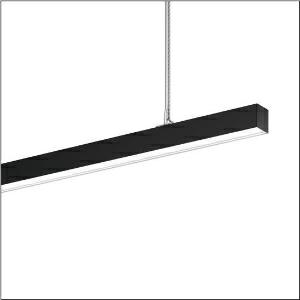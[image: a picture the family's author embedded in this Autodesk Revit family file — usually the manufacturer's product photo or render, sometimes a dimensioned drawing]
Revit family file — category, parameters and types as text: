
# Revit family: silica_r__21_51mx30tbt5b_11dd
name_source: partatom
category: Lighting Fixtures
units: mm (PartAtom-declared; Revit-internal decimal feet)

## family parameters
Cut with Voids When Loaded = No
Host = Face
Light Source = No
Part Type = Normal
Room Calculation Point = No
Round Connector Dimension = Use Diameter
Shared = No

## types (1)
- --- (1 x LED, 5150 lm, 42.2 W, 6500K)
    Apparent Load = 42 VA
    CIE Flux Codes = 47 79 96 58 100
    Color Rendering = 80
    Color Temperature = 6500K
    Default Elevation = 1800 mm
    Description = Silica® 21, office luminaire, primary optical cover: cover, of PMMA, opal, light emission: direct/indirect distribution, primary light characteristic: symmetric, installation type: suspended mounting, LED, rated luminous flux: 5.150lm, luminous efficacy: 116lm/W, light colour: 8tw, colour temperature: 2700..6500K, control gear: ECG DALI, with terminal, 3+2-pole, max. 2.5mm², mains connection: 220..240V, AC, 50/60Hz, rated input power: 44.3W, luminaire housing, of aluminium, jet black (RAL 9005), length: 1.504mm, width: 53mm, height: 53mm, protection rating (complete): IP20, insulation class (complete): insulation class I (protective earthing), certification: CE, permissible operating ambient temperature: 0..+35°C, standard: EN 50419, packaging unit: 1 piece
    Height = 53 mm
    Lamp = 1 x LED
    Lamp Light Flux = 5150 lm
    Lamp Power = 42.2 W
    Lamp count = 1
    Length = 1504 mm
    Luminous efficacy = 122 lm/W
    Manufacturer = Siteco
    ModVariant = No
    Model = 51MX30TBT5B
    Mounting Place = Ceiling
    Mounting Type = Pendant
    Number of Poles = 1
    OnlyDefault = Yes
    Power Factor = 1
    Product Name = Silica® 21
    Product group = office luminaire | ceiling pendant
    ProductGroupID = 902
    Protection Class = Protection class I
    Protection Degree = IP 20
    RLX_Detail_Level = 1
    RLX_Emergency_Light_Flux = 0 lm
    RLX_Emergency_Type = 0
    RLX_Emergency_Type_DB = No
    RlxData = <blob elided: 22881 chars, md5=0ee9e28b>
    Socket = socket
    Standby Power = 0 W
    System Light Flux = 5150 lm
    System Power = 42 W
    Type Comments = individual setting
    Type Image = l_1297744.jpg
    URL = http://relux.com
    VarID = @adj_070957
    Voltage = 0 V
    Weight = 0.00 kg
    Width = 53 mm

## geometry (parser evidence)
native form markers: Blend x4, Sweep x12
no freeform markers — native parametric forms only
